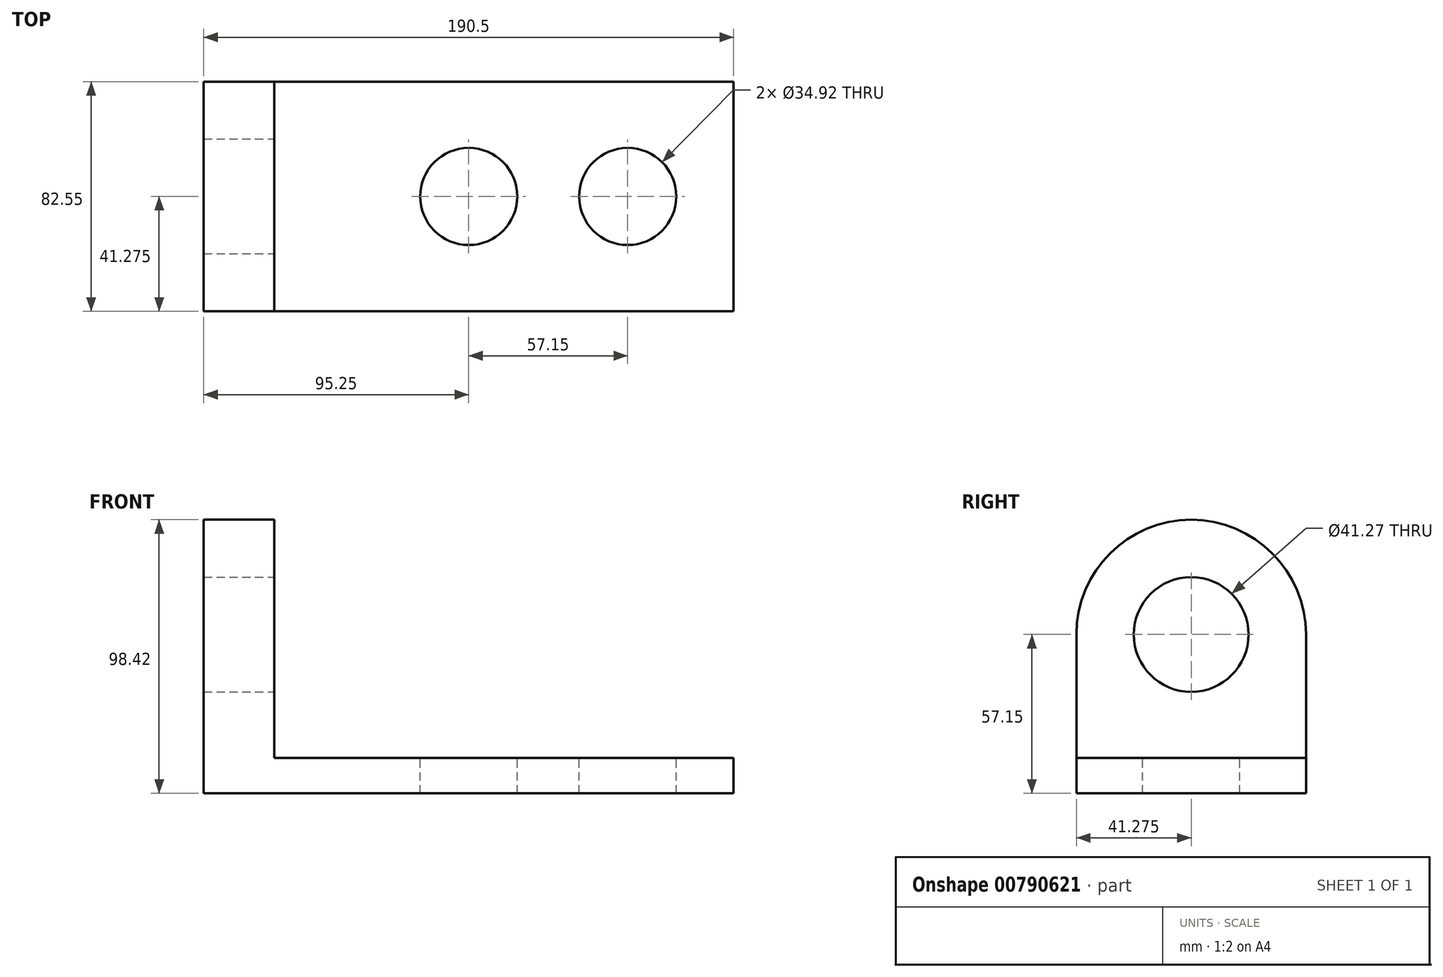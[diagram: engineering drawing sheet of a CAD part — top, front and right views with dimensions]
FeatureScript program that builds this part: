
annotation { "Feature Type Name" : "Feature", "Feature Type Description" : "" }
export const myFeature = defineFeature(function(context is Context, id is Id, definition is map)
    precondition{}
    {
        {
            var Q0;
            Q0=qCreatedBy(makeId("Front.planeOp"),FACE);
            var sketch = newSketch(context, id + "F0", { "sketchPlane" : qUnion([Q0])});
            skLineSegment(sketch, "E0", {"start": v(0, 0) * mm, "end": v(95.25, 0) * mm});
            skLineSegment(sketch, "E1", {"start": v(0, 0) * mm, "end": v(-95.25, 0) * mm});
            skLineSegment(sketch, "E2", {"start": v(95.25, 0) * mm, "end": v(95.25, 12.7) * mm});
            skLineSegment(sketch, "E3", {"start": v(95.25, 12.7) * mm, "end": v(-69.85, 12.7) * mm});
            skLineSegment(sketch, "E4", {"start": v(-95.25, 0) * mm, "end": v(-95.25, 114.3) * mm});
            skLineSegment(sketch, "E5", {"start": v(-95.25, 114.3) * mm, "end": v(-69.85, 114.3) * mm});
            skLineSegment(sketch, "E6", {"start": v(-69.85, 114.3) * mm, "end": v(-69.85, 12.7) * mm});
            skSolve(sketch);
        }
        {
            var Q0;
            Q0=makeQuery(id+"F0.imprint","IMPRINT",FACE,{"disambiguationData":[TD([[makeQuery(id+"F0.imprint","IMPRINT",EDGE,{"derivedFrom":sQuery(id+"F0.wireOp",EDGE,"E0")}),1.0]])]});
            extrude(context, id + "F1", {"entities" : qUnion([Q0]), "depth" : 82.55 * mm, "offsetDistance" : 25.4 * mm});
        }
        {
            var Q0;
            Q0=makeQuery(id+"F1.opExtrude","SWEPT_FACE",FACE,{"disambiguationData":[OSD([sQuery(id+"F0.wireOp",EDGE,"E4")])]});
            var sketch = newSketch(context, id + "F2", { "sketchPlane" : qUnion([Q0])});
            skLineSegment(sketch, "E7", {"start": v(0, 0) * mm, "end": v(0, 57.15) * mm, "construction": true});
            skLineSegment(sketch, "E8", {"start": v(82.55, 0) * mm, "end": v(82.55, 57.15) * mm});
            skArc(sketch, "E9", {"start": v(82.55, 57.15) * mm, "mid": v(41.27, 98.43) * mm, "end": v(0, 57.15) * mm});
            skSolve(sketch);
        }
        {
            var Q0;
            {var subQ0=sQuery(id+"F2.wireOp",EDGE,"E9");Q0=makeQuery(id+"F2.imprint","IMPRINT",FACE,{"disambiguationData":[TD([[makeQuery(id+"F2.imprint","IMPRINT",EDGE,{"derivedFrom":subQ0}),-1.0]])]});}
            extrude(context, id + "F3", {"entities" : qUnion([Q0]), "operationType" : NewBodyOperationType.REMOVE, "oppositeDirection" : true, "depth" : 25.4 * mm, "offsetDistance" : 25.4 * mm});
        }
        {
            var Q0;
            Q0=makeQuery(id+"F1.opExtrude","SWEPT_FACE",FACE,{"disambiguationData":[OSD([sQuery(id+"F0.wireOp",EDGE,"E6")])]});
            var sketch = newSketch(context, id + "F4", { "sketchPlane" : qUnion([Q0])});
            skLineSegment(sketch, "E10", {"start": v(-82.55, 57.15) * mm, "end": v(-41.28, 57.15) * mm, "construction": true});
            skLineSegment(sketch, "E11", {"start": v(-41.28, 57.15) * mm, "end": v(0, 57.15) * mm, "construction": true});
            skCircle(sketch, "E12", {"center": v(-41.28, 57.15) * mm, "radius": 20.64 * mm});
            skSolve(sketch);
        }
        {
            var Q0;
            Q0 = qSketchRegion(id + "F4", true);
            extrude(context, id + "F5", {"entities" : qUnion([Q0]), "operationType" : NewBodyOperationType.REMOVE, "oppositeDirection" : true, "depth" : 25.4 * mm, "offsetDistance" : 25.4 * mm});
        }
        {
            var Q0;
            Q0=makeQuery(id+"F1.opExtrude","SWEPT_FACE",FACE,{"disambiguationData":[OSD([sQuery(id+"F0.wireOp",EDGE,"E3")])]});
            var sketch = newSketch(context, id + "F6", { "sketchPlane" : qUnion([Q0])});
            skLineSegment(sketch, "E13", {"start": v(95.25, -41.28) * mm, "end": v(57.15, -41.28) * mm, "construction": true});
            skLineSegment(sketch, "E14", {"start": v(57.15, -41.28) * mm, "end": v(0, -41.28) * mm, "construction": true});
            skLineSegment(sketch, "E15", {"start": v(0, -41.28) * mm, "end": v(-69.85, -41.28) * mm, "construction": true});
            skCircle(sketch, "E16", {"center": v(57.15, -41.28) * mm, "radius": 17.46 * mm});
            skCircle(sketch, "E17", {"center": v(0, -41.28) * mm, "radius": 17.46 * mm});
            skSolve(sketch);
        }
        {
            var Q0;
            Q0 = qSketchRegion(id + "F6", true);
            extrude(context, id + "F7", {"entities" : qUnion([Q0]), "operationType" : NewBodyOperationType.REMOVE, "oppositeDirection" : true, "depth" : 25.4 * mm, "offsetDistance" : 25.4 * mm});
        }
    });
